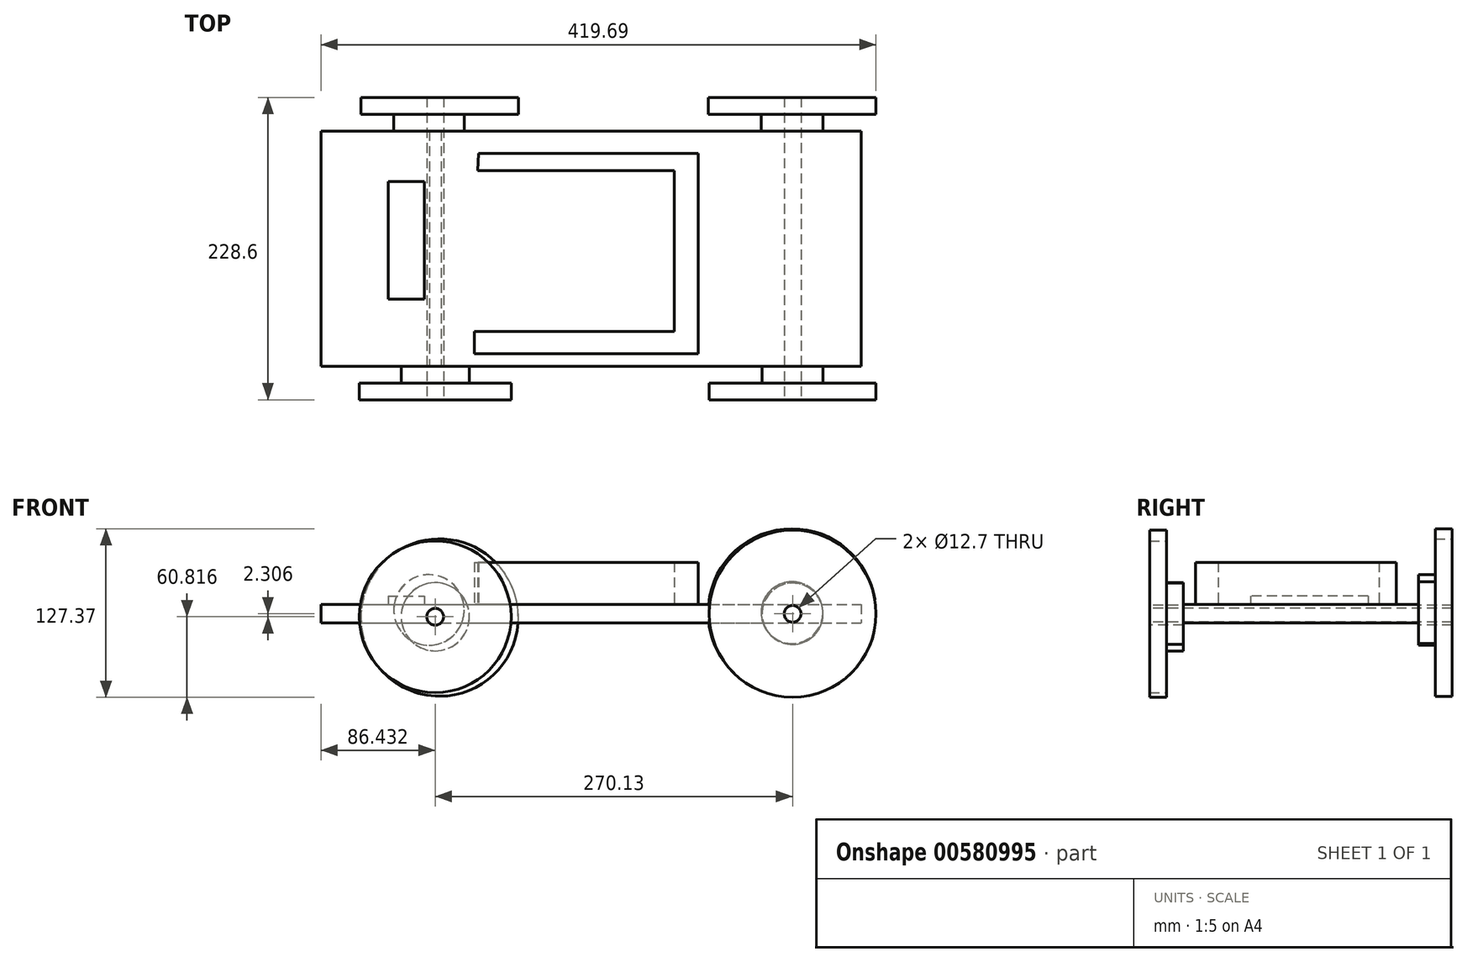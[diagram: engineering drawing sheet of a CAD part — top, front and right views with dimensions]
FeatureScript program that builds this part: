
annotation { "Feature Type Name" : "Feature", "Feature Type Description" : "" }
export const myFeature = defineFeature(function(context is Context, id is Id, definition is map)
    precondition{}
    {
        {
            var Q0;
            Q0=qCreatedBy(makeId("Front.planeOp"),FACE);
            var sketch = newSketch(context, id + "F0", { "sketchPlane" : qUnion([Q0])});
            skCircle(sketch, "E0", {"center": v(-52.1, 44.16) * mm, "radius": 59.46 * mm});
            skSolve(sketch);
        }
        {
            var Q0;
            Q0 = qSketchRegion(id + "F0", true);
            extrude(context, id + "F1", {"entities" : qUnion([Q0]), "depth" : 12.7 * mm, "offsetDistance" : 25.4 * mm});
        }
        {
            var Q0;
            Q0=makeQuery(id+"F1.opExtrude","CAP_FACE",FACE,{"disambiguationData":[OSD([sQuery(id+"F0.wireOp",EDGE,"E0")])],"isStart":false});
            var sketch = newSketch(context, id + "F2", { "sketchPlane" : qUnion([Q0])});
            skCircle(sketch, "E1", {"center": v(-53.35, 43.72) * mm, "radius": 13.86 * mm});
            skSolve(sketch);
        }
        {
            var Q0;
            Q0=makeQuery(id+"F2.imprint","IMPRINT",FACE,{"disambiguationData":[TD([[makeQuery(id+"F2.imprint","IMPRINT",EDGE,{"derivedFrom":sQuery(id+"F2.wireOp",EDGE,"E1")}),-1.0]])]});
            var sketch = newSketch(context, id + "F3", { "sketchPlane" : qUnion([Q0])});
            skCircle(sketch, "E2", {"center": v(-60.16, 49.9) * mm, "radius": 26.63 * mm});
            skSolve(sketch);
        }
        {
            var Q0;
            Q0 = qSketchRegion(id + "F3", true);
            extrude(context, id + "F4", {"entities" : qUnion([Q0]), "operationType" : NewBodyOperationType.ADD, "depth" : 12.7 * mm, "offsetDistance" : 25.4 * mm});
        }
        {
            var Q0;
            Q0=makeQuery(id+"F4.opExtrude","CAP_FACE",FACE,{"disambiguationData":[OSD([sQuery(id+"F3.wireOp",EDGE,"E2")])],"isStart":false});
            var sketch = newSketch(context, id + "F5", { "sketchPlane" : qUnion([Q0])});
            skLineSegment(sketch, "E3.bottom", {"start": v(-141.86, 54.2) * mm, "end": v(266.55, 54.2) * mm});
            skLineSegment(sketch, "E3.top", {"start": v(-141.86, 40.22) * mm, "end": v(266.55, 40.22) * mm});
            skLineSegment(sketch, "E3.left", {"start": v(-141.86, 54.2) * mm, "end": v(-141.86, 40.22) * mm});
            skLineSegment(sketch, "E3.right", {"start": v(266.55, 54.2) * mm, "end": v(266.55, 40.22) * mm});
            skSolve(sketch);
        }
        {
            var Q0;
            Q0 = qSketchRegion(id + "F5", true);
            extrude(context, id + "F6", {"entities" : qUnion([Q0]), "operationType" : NewBodyOperationType.ADD, "depth" : 177.8 * mm, "offsetDistance" : 25.4 * mm});
        }
        {
            var Q0;
            Q0=makeQuery(id+"F6.opExtrude","CAP_FACE",FACE,{"disambiguationData":[OSD([sQuery(id+"F5.wireOp",EDGE,"E3.bottom"),sQuery(id+"F5.wireOp",EDGE,"E3.top"),sQuery(id+"F5.wireOp",EDGE,"E3.left"),sQuery(id+"F5.wireOp",EDGE,"E3.right")])],"isStart":false});
            var sketch = newSketch(context, id + "F7", { "sketchPlane" : qUnion([Q0])});
            skCircle(sketch, "E4", {"center": v(-55.43, 44.74) * mm, "radius": 25.77 * mm});
            skSolve(sketch);
        }
        {
            var Q0;
            Q0 = qSketchRegion(id + "F7", true);
            extrude(context, id + "F8", {"entities" : qUnion([Q0]), "operationType" : NewBodyOperationType.ADD, "depth" : 12.7 * mm, "offsetDistance" : 25.4 * mm});
        }
        {
            var Q0;
            Q0=makeQuery(id+"F8.opExtrude","CAP_FACE",FACE,{"disambiguationData":[OSD([sQuery(id+"F7.wireOp",EDGE,"E4")])],"isStart":false});
            var sketch = newSketch(context, id + "F9", { "sketchPlane" : qUnion([Q0])});
            skCircle(sketch, "E5", {"center": v(-55.43, 44.74) * mm, "radius": 57.38 * mm});
            skSolve(sketch);
        }
        {
            var Q0;
            Q0 = qSketchRegion(id + "F9", true);
            extrude(context, id + "F10", {"entities" : qUnion([Q0]), "operationType" : NewBodyOperationType.ADD, "depth" : 12.7 * mm, "offsetDistance" : 25.4 * mm});
        }
        {
            var Q0;
            Q0=makeQuery(id+"F6.opExtrude","SWEPT_FACE",FACE,{"disambiguationData":[OSD([sQuery(id+"F5.wireOp",EDGE,"E3.bottom")])]});
            var sketch = newSketch(context, id + "F11", { "sketchPlane" : qUnion([Q0])});
            skLineSegment(sketch, "E6.bottom", {"start": v(-91.06, -63.5) * mm, "end": v(-63.65, -63.5) * mm});
            skLineSegment(sketch, "E6.top", {"start": v(-91.06, -152.4) * mm, "end": v(-63.65, -152.4) * mm});
            skLineSegment(sketch, "E6.left", {"start": v(-91.06, -63.5) * mm, "end": v(-91.06, -152.4) * mm});
            skLineSegment(sketch, "E6.right", {"start": v(-63.65, -63.5) * mm, "end": v(-63.65, -152.4) * mm});
            skSolve(sketch);
        }
        {
            var Q0;
            Q0 = qSketchRegion(id + "F11", true);
            extrude(context, id + "F12", {"entities" : qUnion([Q0]), "operationType" : NewBodyOperationType.ADD, "depth" : 6.35 * mm, "offsetDistance" : 25.4 * mm});
        }
        {
            var Q0;
            {var subQ1=sQuery(id+"F5.wireOp",EDGE,"E3.right");var subQ2=sQuery(id+"F5.wireOp",EDGE,"E3.top");var subQ3=sQuery(id+"F5.wireOp",EDGE,"E3.bottom");Q0=makeQuery(id+"F8.boolean.opBoolean","SPLIT",FACE,{"disambiguationData":[TD([makeQuery(id+"F6.opExtrude","SWEPT_FACE",FACE,{"disambiguationData":[OSD([subQ1])]})])],"derivedFrom":makeQuery(id+"F6.opExtrude","CAP_FACE",FACE,{"disambiguationData":[OSD([subQ3,subQ2,sQuery(id+"F5.wireOp",EDGE,"E3.left"),subQ1])],"isStart":false})});}
            var sketch = newSketch(context, id + "F13", { "sketchPlane" : qUnion([Q0])});
            skCircle(sketch, "E7", {"center": v(214.7, 47.04) * mm, "radius": 23.1 * mm});
            skSolve(sketch);
        }
        {
            var Q0;
            Q0 = qSketchRegion(id + "F13", true);
            extrude(context, id + "F14", {"entities" : qUnion([Q0]), "operationType" : NewBodyOperationType.ADD, "depth" : 12.7 * mm, "offsetDistance" : 25.4 * mm});
        }
        {
            var Q0;
            Q0=makeQuery(id+"F14.opExtrude","CAP_FACE",FACE,{"disambiguationData":[OSD([sQuery(id+"F13.wireOp",EDGE,"E7")])],"isStart":false});
            var sketch = newSketch(context, id + "F15", { "sketchPlane" : qUnion([Q0])});
            skCircle(sketch, "E8", {"center": v(214.7, 47.04) * mm, "radius": 63.13 * mm});
            skSolve(sketch);
        }
        {
            var Q0;
            Q0 = qSketchRegion(id + "F15", true);
            extrude(context, id + "F16", {"entities" : qUnion([Q0]), "operationType" : NewBodyOperationType.ADD, "depth" : 12.7 * mm, "offsetDistance" : 25.4 * mm});
        }
        {
            var Q0;
            {var subQ0=sQuery(id+"F5.wireOp",EDGE,"E3.bottom");var subQ1=sQuery(id+"F5.wireOp",EDGE,"E3.top");var subQ3=sQuery(id+"F5.wireOp",EDGE,"E3.right");Q0=makeQuery(id+"F6.boolean.opBoolean","SPLIT",FACE,{"disambiguationData":[TD([makeQuery(id+"F6.opExtrude","SWEPT_FACE",FACE,{"disambiguationData":[OSD([subQ3])]})])],"derivedFrom":makeQuery(id+"F6.opExtrude","CAP_FACE",FACE,{"disambiguationData":[OSD([subQ0,subQ1,sQuery(id+"F5.wireOp",EDGE,"E3.left"),subQ3])],"isStart":true})});}
            var sketch = newSketch(context, id + "F17", { "sketchPlane" : qUnion([Q0])});
            skCircle(sketch, "E9", {"center": v(-214.27, 47.87) * mm, "radius": 23.35 * mm});
            skSolve(sketch);
        }
        {
            var Q0;
            Q0 = qSketchRegion(id + "F17", true);
            extrude(context, id + "F18", {"entities" : qUnion([Q0]), "operationType" : NewBodyOperationType.ADD, "depth" : 12.7 * mm, "offsetDistance" : 25.4 * mm});
        }
        {
            var Q0;
            Q0=makeQuery(id+"F18.opExtrude","CAP_FACE",FACE,{"disambiguationData":[OSD([sQuery(id+"F17.wireOp",EDGE,"E9")])],"isStart":false});
            var sketch = newSketch(context, id + "F19", { "sketchPlane" : qUnion([Q0])});
            skCircle(sketch, "E10", {"center": v(-214.27, 47.87) * mm, "radius": 63.42 * mm});
            skSolve(sketch);
        }
        {
            var Q0;
            Q0 = qSketchRegion(id + "F19", true);
            extrude(context, id + "F20", {"entities" : qUnion([Q0]), "operationType" : NewBodyOperationType.ADD, "depth" : 12.7 * mm, "offsetDistance" : 25.4 * mm});
        }
        {
            var Q0;
            Q0=makeQuery(id+"F6.opExtrude","SWEPT_FACE",FACE,{"disambiguationData":[OSD([sQuery(id+"F5.wireOp",EDGE,"E3.bottom")])]});
            var sketch = newSketch(context, id + "F21", { "sketchPlane" : qUnion([Q0])});
            skLineSegment(sketch, "E11", {"start": v(-22.58, -42.23) * mm, "end": v(143.31, -42.23) * mm});
            skLineSegment(sketch, "E12", {"start": v(143.31, -42.23) * mm, "end": v(143.31, -193.85) * mm});
            skLineSegment(sketch, "E13", {"start": v(143.31, -193.85) * mm, "end": v(-25.9, -193.85) * mm});
            skLineSegment(sketch, "E14", {"start": v(-25.9, -193.85) * mm, "end": v(-25.9, -176.85) * mm});
            skLineSegment(sketch, "E15", {"start": v(-25.9, -176.85) * mm, "end": v(125.42, -176.85) * mm});
            skLineSegment(sketch, "E16", {"start": v(125.42, -176.85) * mm, "end": v(125.42, -55.22) * mm});
            skLineSegment(sketch, "E17", {"start": v(125.42, -55.22) * mm, "end": v(-23.33, -55.22) * mm});
            skLineSegment(sketch, "E18", {"start": v(-23.33, -55.22) * mm, "end": v(-22.58, -42.23) * mm});
            skSolve(sketch);
        }
        {
            var Q0;
            Q0 = qSketchRegion(id + "F21", true);
            extrude(context, id + "F22", {"entities" : qUnion([Q0]), "operationType" : NewBodyOperationType.ADD, "depth" : 31.75 * mm, "offsetDistance" : 25.4 * mm});
        }
        {
            var Q0;
            Q0=makeQuery(id+"F10.opExtrude","CAP_FACE",FACE,{"disambiguationData":[OSD([sQuery(id+"F9.wireOp",EDGE,"E5")])],"isStart":false});
            var sketch = newSketch(context, id + "F23", { "sketchPlane" : qUnion([Q0])});
            skPoint(sketch, "E19", {"position": v(-55.43, 44.74) * mm});
            skSolve(sketch);
        }
        {
            var Q0;
            Q0=sQuery(id+"F23.wireOp",VERTEX,"E19");
            var Q1;
            Q1=makeQuery(id+"F1.opExtrude","SWEPT_BODY",BODY,{"disambiguationData":[OSD([sQuery(id+"F0.wireOp",EDGE,"E0")])]});
            hole(context, id + "F24", {"style" : HoleStyle.SIMPLE, "endStyle" : HoleEndStyle.THROUGH, "holeDiameter" : 12.7 * mm, "majorDiameter" : 6.35 * mm, "isTappedThrough" : true, "tappedDepth" : 12.7 * mm, "tapClearance" : 3, "locations" : qUnion([Q0]), "scope" : qUnion([Q1])});
        }
        {
            var Q0;
            Q0=makeQuery(id+"F16.opExtrude","CAP_FACE",FACE,{"disambiguationData":[OSD([sQuery(id+"F15.wireOp",EDGE,"E8")])],"isStart":false});
            var sketch = newSketch(context, id + "F25", { "sketchPlane" : qUnion([Q0])});
            skPoint(sketch, "E20", {"position": v(214.7, 47.04) * mm});
            skSolve(sketch);
        }
        {
            var Q0;
            Q0=sQuery(id+"F25.wireOp",VERTEX,"E20");
            var Q1;
            Q1=makeQuery(id+"F1.opExtrude","SWEPT_BODY",BODY,{"disambiguationData":[OSD([sQuery(id+"F0.wireOp",EDGE,"E0")])]});
            hole(context, id + "F26", {"style" : HoleStyle.SIMPLE, "endStyle" : HoleEndStyle.THROUGH, "holeDiameter" : 12.7 * mm, "majorDiameter" : 6.35 * mm, "isTappedThrough" : true, "tappedDepth" : 12.7 * mm, "tapClearance" : 3, "locations" : qUnion([Q0]), "scope" : qUnion([Q1])});
        }
    });
